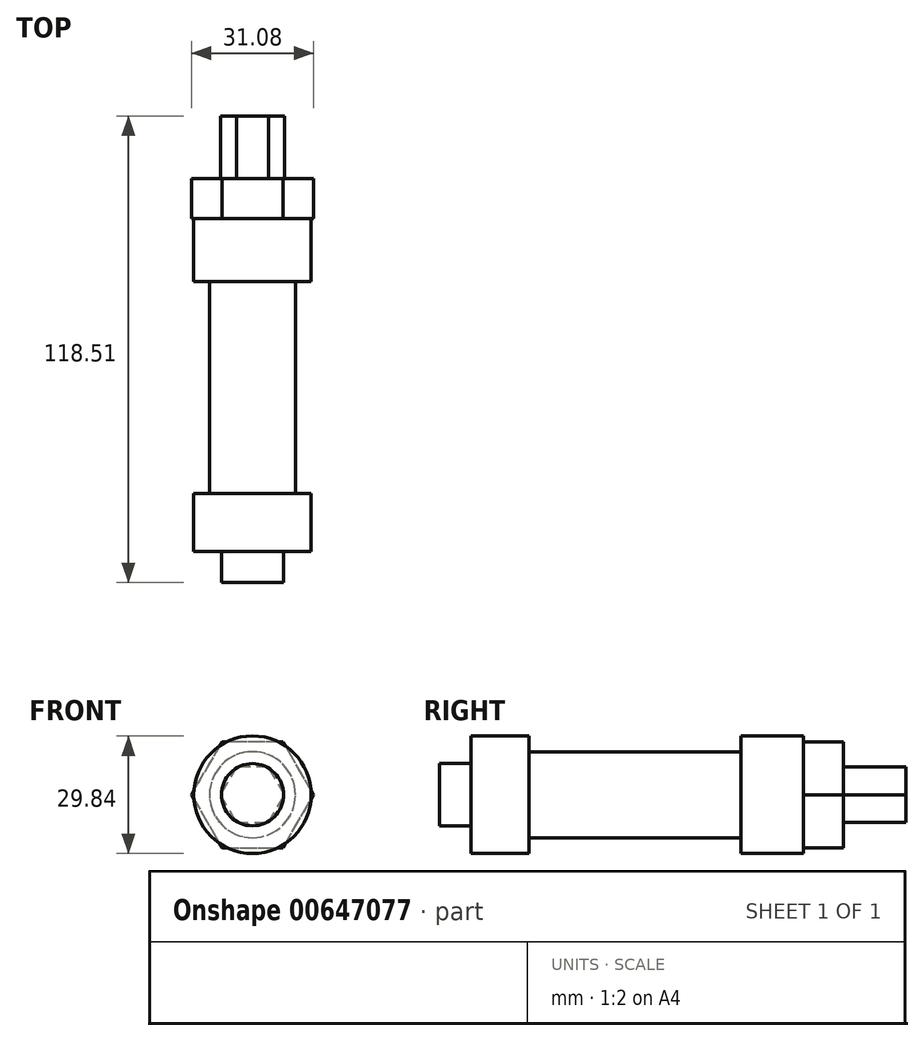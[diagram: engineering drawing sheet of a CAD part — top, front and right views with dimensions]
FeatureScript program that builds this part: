
annotation { "Feature Type Name" : "Feature", "Feature Type Description" : "" }
export const myFeature = defineFeature(function(context is Context, id is Id, definition is map)
    precondition{}
    {
        {
            var Q0;
            Q0=qCreatedBy(makeId("Front.planeOp"),FACE);
            var sketch = newSketch(context, id + "F0", { "sketchPlane" : qUnion([Q0])});
            skCircle(sketch, "E0", {"center": v(0, 0) * mm, "radius": 10.92 * mm});
            skSolve(sketch);
        }
        {
            var Q0;
            Q0 = qSketchRegion(id + "F0", true);
            extrude(context, id + "F1", {"entities" : qUnion([Q0]), "depth" : 68.58 * mm, "offsetDistance" : 25.4 * mm});
        }
        {
            var Q0;
            Q0=makeQuery(id+"F1.opExtrude","CAP_FACE",FACE,{"disambiguationData":[OSD([sQuery(id+"F0.wireOp",EDGE,"E0")])],"isStart":true});
            var sketch = newSketch(context, id + "F2", { "sketchPlane" : qUnion([Q0])});
            skCircle(sketch, "E1", {"center": v(0, 0) * mm, "radius": 14.92 * mm});
            skSolve(sketch);
        }
        {
            var Q0;
            Q0 = qSketchRegion(id + "F2", true);
            var Q1;
            Q1=makeQuery(id+"F1.opExtrude","CAP_FACE",FACE,{"disambiguationData":[OSD([sQuery(id+"F0.wireOp",EDGE,"E0")])],"isStart":false});
            extrude(context, id + "F3", {"entities" : qUnion([Q0, Q1]), "operationType" : NewBodyOperationType.ADD, "oppositeDirection" : true, "depth" : 15.95 * mm, "offsetDistance" : 25.4 * mm});
        }
        {
            var Q0;
            Q0=makeQuery(id+"F3.opExtrude","CAP_FACE",FACE,{"disambiguationData":[OSD([sQuery(id+"F0.wireOp",EDGE,"E0")])],"isStart":false});
            var sketch = newSketch(context, id + "F4", { "sketchPlane" : qUnion([Q0])});
            skCircle(sketch, "E2", {"center": v(0, 0) * mm, "radius": 14.92 * mm});
            skSolve(sketch);
        }
        {
            var Q0;
            Q0 = qSketchRegion(id + "F4", true);
            extrude(context, id + "F5", {"entities" : qUnion([Q0]), "operationType" : NewBodyOperationType.ADD, "oppositeDirection" : true, "depth" : 14.73 * mm, "offsetDistance" : 25.4 * mm});
        }
        {
            var Q0;
            Q0=makeQuery(id+"F5.boolean.opBoolean","MERGE",FACE,{"derivedFrom":[makeQuery(id+"F3.opExtrude","CAP_FACE",FACE,{"disambiguationData":[OSD([sQuery(id+"F0.wireOp",EDGE,"E0")])],"isStart":false}),makeQuery(id+"F5.opExtrude","CAP_FACE",FACE,{"disambiguationData":[OSD([sQuery(id+"F4.wireOp",EDGE,"E2")])],"isStart":true})]});
            var sketch = newSketch(context, id + "F6", { "sketchPlane" : qUnion([Q0])});
            skCircle(sketch, "E3", {"center": v(0, 0) * mm, "radius": 7.9 * mm});
            skSolve(sketch);
        }
        {
            var Q0;
            Q0 = qSketchRegion(id + "F6", true);
            var Q1;
            Q1=makeQuery(id+"F3.boolean.opBoolean","MERGE",FACE,{"derivedFrom":[makeQuery(id+"F1.opExtrude","CAP_FACE",FACE,{"disambiguationData":[OSD([sQuery(id+"F0.wireOp",EDGE,"E0")])],"isStart":true}),makeQuery(id+"F3.opExtrude","CAP_FACE",FACE,{"disambiguationData":[OSD([sQuery(id+"F2.wireOp",EDGE,"E1")])],"isStart":true})]});
            extrude(context, id + "F7", {"entities" : qUnion([Q0, Q1]), "operationType" : NewBodyOperationType.ADD, "depth" : 7.94 * mm, "offsetDistance" : 25.4 * mm});
        }
        {
            var Q0;
            Q0=makeQuery(id+"F3.boolean.opBoolean","MERGE",FACE,{"derivedFrom":[makeQuery(id+"F1.opExtrude","CAP_FACE",FACE,{"disambiguationData":[OSD([sQuery(id+"F0.wireOp",EDGE,"E0")])],"isStart":true}),makeQuery(id+"F3.opExtrude","CAP_FACE",FACE,{"disambiguationData":[OSD([sQuery(id+"F2.wireOp",EDGE,"E1")])],"isStart":true})]});
            var sketch = newSketch(context, id + "F8", { "sketchPlane" : qUnion([Q0])});
            skCircle(sketch, "E4.cCircle", {"center": v(0, 0) * mm, "radius": 13.46 * mm, "construction": true});
            skLineSegment(sketch, "E4.0", {"start": v(7.77, -13.46) * mm, "end": v(-7.77, -13.46) * mm});
            skLineSegment(sketch, "E4.1", {"start": v(-7.77, -13.46) * mm, "end": v(-15.54, 0) * mm});
            skLineSegment(sketch, "E4.2", {"start": v(-15.54, 0) * mm, "end": v(-7.77, 13.46) * mm});
            skLineSegment(sketch, "E4.3", {"start": v(-7.77, 13.46) * mm, "end": v(7.77, 13.46) * mm});
            skLineSegment(sketch, "E4.4", {"start": v(7.77, 13.46) * mm, "end": v(15.54, 0) * mm});
            skLineSegment(sketch, "E4.5", {"start": v(15.54, 0) * mm, "end": v(7.77, -13.46) * mm});
            skPoint(sketch, "E4.0.midPoint", {"position": v(0, -13.46) * mm});
            skSolve(sketch);
        }
        {
            var Q0;
            Q0 = qSketchRegion(id + "F8", true);
            extrude(context, id + "F9", {"entities" : qUnion([Q0]), "operationType" : NewBodyOperationType.ADD, "depth" : 10.16 * mm, "offsetDistance" : 25.4 * mm});
        }
        {
            var Q0;
            Q0=makeQuery(id+"F9.opExtrude","CAP_FACE",FACE,{"disambiguationData":[OSD([sQuery(id+"F8.wireOp",EDGE,"E4.0"),sQuery(id+"F8.wireOp",EDGE,"E4.1"),sQuery(id+"F8.wireOp",EDGE,"E4.2"),sQuery(id+"F8.wireOp",EDGE,"E4.3"),sQuery(id+"F8.wireOp",EDGE,"E4.4"),sQuery(id+"F8.wireOp",EDGE,"E4.5")])],"isStart":false});
            var sketch = newSketch(context, id + "F10", { "sketchPlane" : qUnion([Q0])});
            skCircle(sketch, "E5.cCircle", {"center": v(0, 0) * mm, "radius": 7.08 * mm, "construction": true});
            skLineSegment(sketch, "E5.0", {"start": v(4.09, -7.08) * mm, "end": v(-4.09, -7.08) * mm});
            skLineSegment(sketch, "E5.1", {"start": v(-4.09, -7.08) * mm, "end": v(-8.18, 0) * mm});
            skLineSegment(sketch, "E5.2", {"start": v(-8.18, 0) * mm, "end": v(-4.09, 7.08) * mm});
            skLineSegment(sketch, "E5.3", {"start": v(-4.09, 7.08) * mm, "end": v(4.09, 7.08) * mm});
            skLineSegment(sketch, "E5.4", {"start": v(4.09, 7.08) * mm, "end": v(8.18, 0) * mm});
            skLineSegment(sketch, "E5.5", {"start": v(8.18, 0) * mm, "end": v(4.09, -7.08) * mm});
            skPoint(sketch, "E5.0.midPoint", {"position": v(0, -7.08) * mm});
            skSolve(sketch);
        }
        {
            var Q0;
            Q0 = qSketchRegion(id + "F10", true);
            extrude(context, id + "F11", {"entities" : qUnion([Q0]), "operationType" : NewBodyOperationType.ADD, "depth" : 15.88 * mm, "offsetDistance" : 25.4 * mm});
        }
    });
